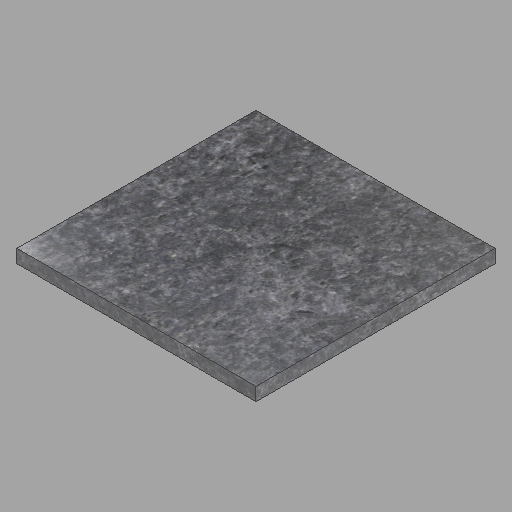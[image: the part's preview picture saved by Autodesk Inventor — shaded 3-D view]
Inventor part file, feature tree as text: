
AUTODESK INVENTOR PART (.ipt)
format: ipt  version: 2023 (Build 270158000, 158)  size: 247,808 bytes
history: native  units: in
note: dims shown in document units (in); Inventor stores cm internally (conversion verified against a paired STEP export)
features: other x1, extrude x1, sketch x1
ambient origin geometry x8: Origin, YZ Plane, XZ Plane, XY Plane, X Axis, Y Axis, Z Axis, Center Point
bodies: Solid1 (feature_tree)
feature tree (3):
  other  "18x18x2-77"
  extrude  "Extrusion1"  Depth=18.0in
  sketch  "Sketch1"  dims[d0=18.0in d1=18.0in d2=1.0in d3=0.0in]
